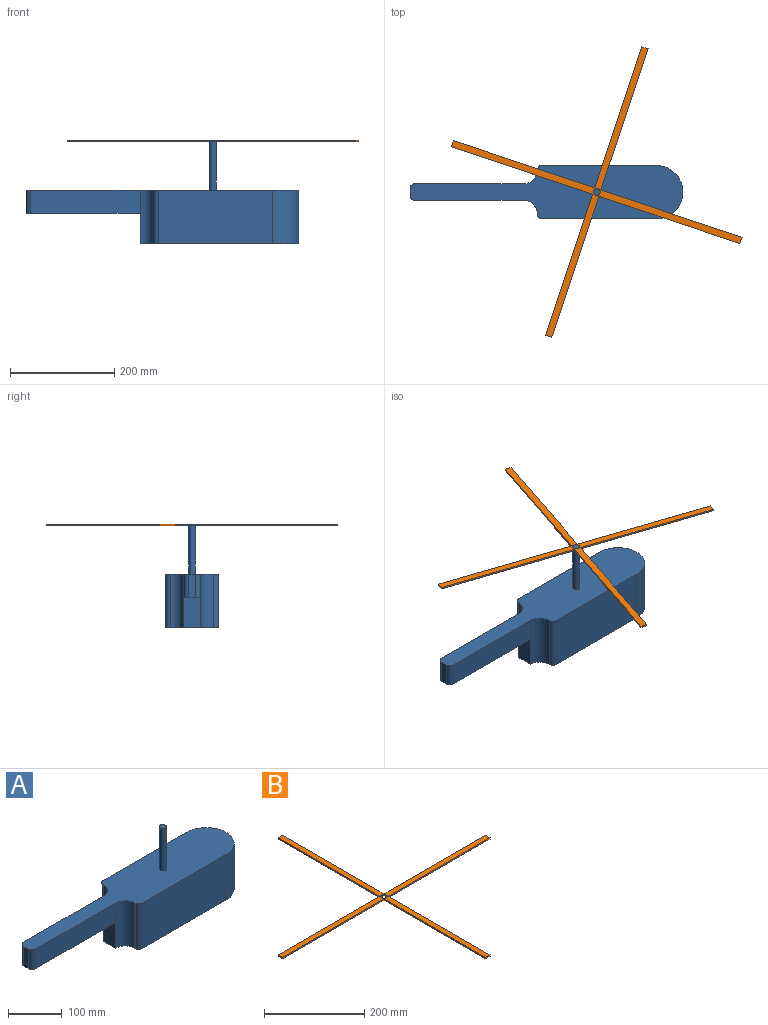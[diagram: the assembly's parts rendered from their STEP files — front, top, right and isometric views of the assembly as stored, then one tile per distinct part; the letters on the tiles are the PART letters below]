
ASSEMBLY  parts=2 mates=1
PART A: 20 faces, bbox 524.4x102.4x198.6 mm
  f0: plane 58.67x31.85mm, normal (-1,0,0), area 1868.9mm2, adj f5,f6,f11,f17
  f1: cylinder r=51.22mm len=102.87mm, axis (0,0,-1), area 16552.8mm2, adj f2,f9,f10,f11
  f2: plane 219.33x102.87mm, normal (0,1,0), area 22562.4mm2, adj f1,f3,f10,f11
  f3: cylinder r=9.42mm len=102.87mm, axis (0,0,-1), area 1522.7mm2, adj f2,f4,f10,f11
  f4: plane 102.87x0.47mm, normal (-1,0,0), area 48.3mm2, adj f3,f5,f10,f11
  f5: cylinder r=25.4mm len=102.87mm, axis (0,0,-1), area 4104.3mm2, adj f0,f4,f10,f11,f12
  f6: cylinder r=25.4mm len=102.87mm, axis (0,0,-1), area 4104.3mm2, adj f0,f7,f10,f11,f16
  f7: plane 102.87x0.47mm, normal (-1,0,0), area 48.3mm2, adj f6,f8,f10,f11
  f8: cylinder r=9.42mm len=102.87mm, axis (0,0,-1), area 1522.7mm2, adj f7,f9,f10,f11
  f9: plane 219.33x102.87mm, normal (0,-1,0), area 22562.4mm2, adj f1,f8,f10,f11
  f10: plane 524.45x102.44mm, normal (0,0,1), area 35407.5mm2, adj f1,f2,f3,f4,f5,f6,f7,f8
  f11: plane 305.37x102.44mm, normal (0,0,-1), area 28601.6mm2, adj f0,f1,f2,f3,f4,f5,f6,f7
  f12: plane 209.65x44.2mm, normal (0,1,0), area 9265.8mm2, adj f5,f10,f13,f17
  f13: cylinder r=9.42mm len=44.2mm, axis (0,0,1), area 654.2mm2, adj f10,f12,f14,f17
  f14: plane 44.2x13mm, normal (-1,0,0), area 574.8mm2, adj f10,f13,f15,f17
  f15: cylinder r=9.42mm len=44.2mm, axis (0,0,1), area 654.2mm2, adj f10,f14,f16,f17
  f16: plane 209.65x44.2mm, normal (0,-1,0), area 9265.8mm2, adj f6,f10,f15,f17
  f17: plane 219.08x31.85mm, normal (0,0,-1), area 6939.8mm2, adj f0,f12,f13,f14,f15,f16
  f18: cylinder r=6.53mm len=95.76mm, axis (0,0,-1), area 3928.4mm2, adj f10,f19
  f19: plane 13.06x13.06mm, normal (0,0,1), area 133.9mm2, adj f18
PART B: 22 faces, bbox 584.2x584.2x3.2 mm
  f0: plane 285.75x3.18mm, normal (0,-1,0), area 907.3mm2, adj f1,f19,f20,f21
  f1: plane 285.75x3.18mm, normal (-1,0,0), area 907.3mm2, adj f0,f2,f20,f21
  f2: plane 12.7x3.18mm, normal (0,-1,0), area 40.3mm2, adj f1,f3,f20,f21
  f3: plane 285.75x3.18mm, normal (1,0,0), area 907.3mm2, adj f2,f4,f20,f21
  f4: plane 285.75x3.18mm, normal (0,-1,0), area 907.3mm2, adj f3,f5,f20,f21
  f5: plane 12.7x3.18mm, normal (1,0,0), area 40.3mm2, adj f4,f6,f20,f21
  f6: plane 285.75x3.18mm, normal (0,1,0), area 907.3mm2, adj f5,f7,f20,f21
  f7: plane 285.75x3.18mm, normal (1,0,0), area 907.3mm2, adj f6,f8,f20,f21
  f8: plane 12.7x3.18mm, normal (0,1,0), area 40.3mm2, adj f7,f9,f20,f21
  f9: plane 285.75x3.18mm, normal (-1,0,0), area 907.3mm2, adj f8,f10,f20,f21
  f10: plane 285.75x3.18mm, normal (0,1,0), area 907.3mm2, adj f9,f19,f20,f21
  f11: plane 3.18x3.04mm, normal (0,1,0), area 9.6mm2, adj f12,f18,f20,f21
  f12: cylinder r=6.53mm len=4.83mm, axis (0,0,1), area 22.8mm2, adj f11,f13,f20,f21
  f13: plane 3.18x3.04mm, normal (1,0,0), area 9.6mm2, adj f12,f14,f20,f21
  f14: cylinder r=6.53mm len=4.83mm, axis (0,0,1), area 22.8mm2, adj f13,f15,f20,f21
  f15: plane 3.18x3.04mm, normal (0,-1,0), area 9.6mm2, adj f14,f16,f20,f21
  f16: cylinder r=6.53mm len=4.83mm, axis (0,0,1), area 22.8mm2, adj f15,f17,f20,f21
  f17: plane 3.18x3.04mm, normal (-1,0,0), area 9.6mm2, adj f16,f18,f20,f21
  f18: cylinder r=6.53mm len=4.83mm, axis (0,0,1), area 22.8mm2, adj f11,f17,f20,f21
  f19: plane 12.7x3.18mm, normal (-1,0,0), area 40.3mm2, adj f0,f10,f20,f21
  f20: plane 584.2x584.2mm, normal (0,0,-1), area 14544.9mm2, adj f0,f1,f2,f3,f4,f5,f6,f7
  f21: plane 584.2x584.2mm, normal (0,0,1), area 14544.9mm2, adj f0,f1,f2,f3,f4,f5,f6,f7
PLACE A t=(-15,0,0)mm
PLACE B rot(axis=(0,0,-1),108.5deg) t=(-15,0,0)mm
MATE revolute B.f12 <-> A.f18  axis (0,0,1) through (-15,0,198.63)mm
